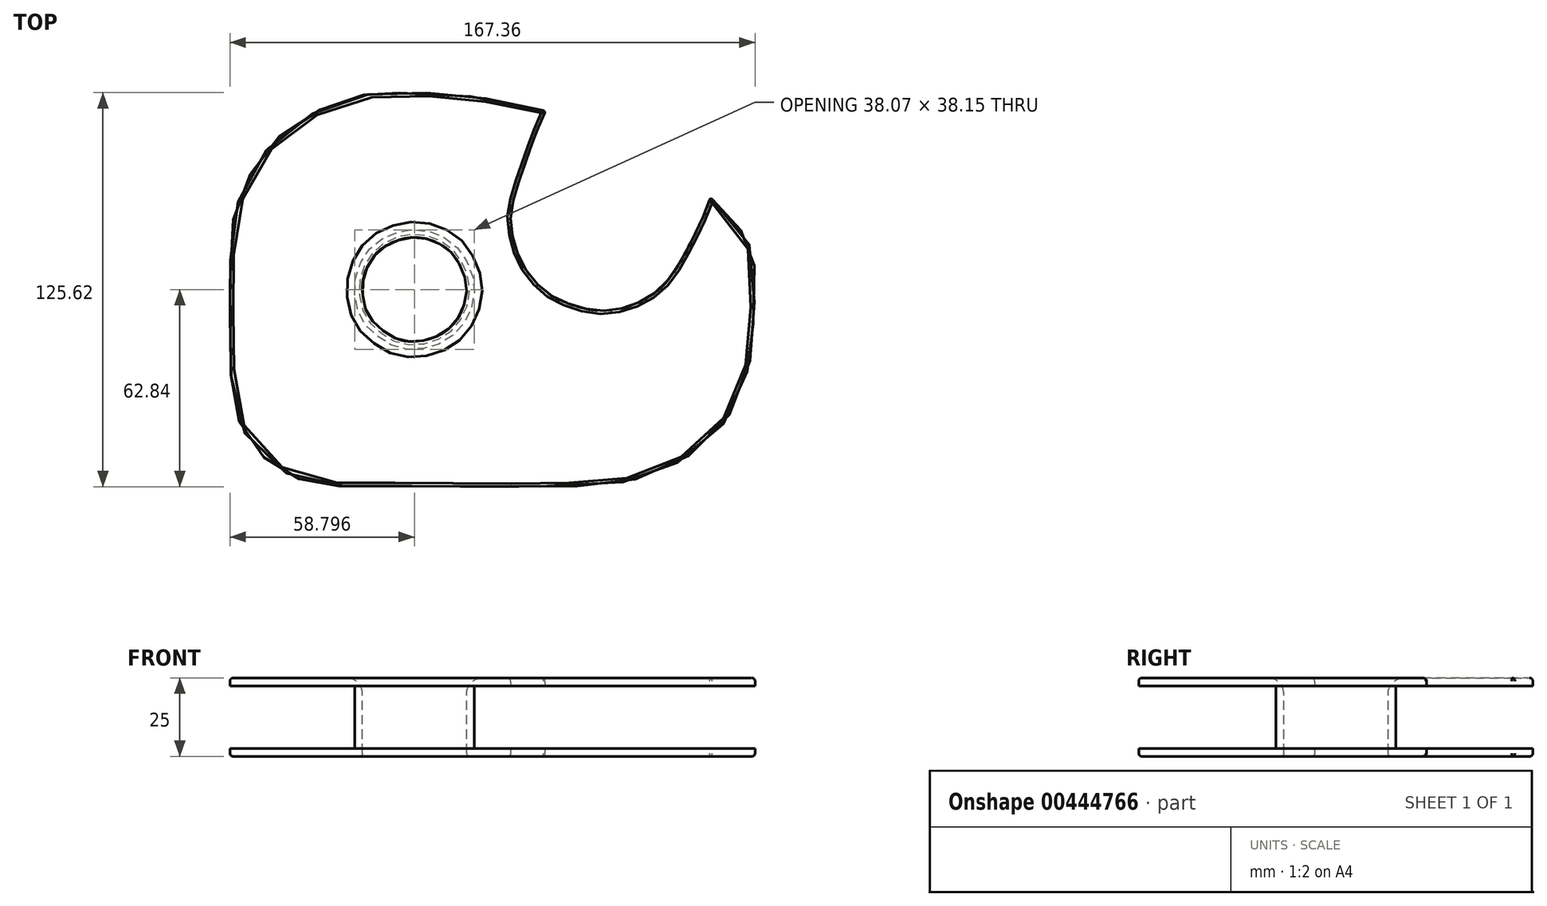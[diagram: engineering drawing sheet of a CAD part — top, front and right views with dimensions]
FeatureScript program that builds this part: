
annotation { "Feature Type Name" : "Feature", "Feature Type Description" : "" }
export const myFeature = defineFeature(function(context is Context, id is Id, definition is map)
    precondition{}
    {
        {
            var Q0;
            Q0=qCreatedBy(makeId("Top.planeOp"),FACE);
            var sketch = newSketch(context, id + "F0", { "sketchPlane" : qUnion([Q0])});
            skFitSpline(sketch, "E0", {"points": [v(45.99, 21.9) * mm, v(12.9, 27.42) * mm, v(-3.47, 27.42) * mm, v(-9.9, 27.14) * mm, v(-16.8, 25.67) * mm, v(-30.69, 19.42) * mm, v(-39.88, 12.25) * mm, v(-47.05, 2.69) * mm, v(-52.38, -10) * mm, v(-53.86, -22.32) * mm, v(-53.67, -64.06) * mm, v(-51.83, -75.46) * mm, v(-47.05, -84.56) * mm, v(-40.07, -91.18) * mm, v(-31.97, -95.4) * mm, v(-21.86, -97.62) * mm, v(-14.32, -97.7) * mm, v(54.72, -97.7) * mm, v(78.17, -94.67) * mm, v(95.82, -85.48) * mm, v(107.22, -71.14) * mm, v(112, -55.42) * mm, v(112.83, -43.65) * mm, v(112.88, -25.44) * mm, v(110.14, -18.34) * mm, v(105.55, -12.2) * mm, v(99.18, -6.12) * mm, v(98.6, -7.16) * mm, v(92.37, -20.85) * mm, v(84.82, -32.92) * mm, v(77.94, -38.25) * mm, v(68.68, -41.5) * mm, v(61.06, -41.5) * mm, v(54.61, -39.8) * mm, v(48.1, -36.84) * mm, v(43.44, -32.77) * mm, v(38.62, -25.96) * mm, v(35.44, -14.12) * mm, v(37.3, -3.01) * mm, v(45.73, 20.23) * mm, v(45.99, 21.9) * mm]});
            skFitSpline(sketch, "E1", {"points": [v(-8, -24.14) * mm, v(-4.79, -21.34) * mm, v(1.77, -18.71) * mm, v(9.22, -19.07) * mm, v(16.08, -22.89) * mm, v(19.65, -28.25) * mm, v(21.32, -34.45) * mm, v(19.65, -42.2) * mm, v(15.36, -47.8) * mm, v(8.92, -51.02) * mm, v(0.58, -51.26) * mm, v(-5.15, -48.22) * mm, v(-9.14, -44.58) * mm, v(-11.35, -39.52) * mm, v(-11.82, -33.38) * mm, v(-10.63, -28.55) * mm, v(-8, -24.14) * mm]});
            skSolve(sketch);
        }
        {
            var Q0;
            Q0 = qSketchRegion(id + "F0", true);
            extrude(context, id + "F1", {"entities" : qUnion([Q0]), "depth" : 25 * mm});
        }
        {
            var Q0;
            Q0=makeQuery(id+"F1.opExtrude","SWEPT_FACE",FACE,{"disambiguationData":[OSD([sQuery(id+"F0.wireOp",EDGE,"E0")])]});
            shell(context, id + "F2", {"entities" : qUnion([Q0]), "thickness" : 2.5 * mm});
        }
        {
            var Q0;
            Q0=makeQuery(id+"F1.opExtrude","CAP_EDGE",EDGE,{"disambiguationData":[OSD([sQuery(id+"F0.wireOp",EDGE,"E1")])],"isStart":false});
            fillet(context, id + "F3", {"entities" : qUnion([Q0]), "radius" : 5 * mm, "tangentPropagation" : true, "allowEdgeOverflow" : false});
        }
        {
            var Q0;
            Q0=makeQuery(id+"F1.opExtrude","CAP_FACE",FACE,{"disambiguationData":[OSD([sQuery(id+"F0.wireOp",EDGE,"E0"),sQuery(id+"F0.wireOp",EDGE,"E1")])],"isStart":false});
            fillet(context, id + "F4", {"entities" : qUnion([Q0]), "radius" : 1 * mm, "tangentPropagation" : true, "allowEdgeOverflow" : false});
        }
        {
            var Q0;
            Q0=makeQuery(id+"F1.opExtrude","CAP_FACE",FACE,{"disambiguationData":[OSD([sQuery(id+"F0.wireOp",EDGE,"E0"),sQuery(id+"F0.wireOp",EDGE,"E1")])],"isStart":true});
            fillet(context, id + "F5", {"entities" : qUnion([Q0]), "radius" : 1 * mm, "tangentPropagation" : true, "allowEdgeOverflow" : false});
        }
    });
